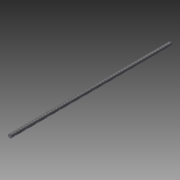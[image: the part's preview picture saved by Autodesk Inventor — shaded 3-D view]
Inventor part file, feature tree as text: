
AUTODESK INVENTOR PART (.ipt)
format: ipt  version: 2014 SP1 (Build 180222100, 222)  size: 68,096 bytes
history: native  units: mm
features: extrude x1, thread x1, sketch x1
ambient origin geometry x8: Origin, YZ Plane, XZ Plane, XY Plane, X Axis, Y Axis, Z Axis, Center Point
bodies: Solid1 (feature_tree)
feature tree (3):
  extrude  "Extrusion1"  Depth=350.0mm TaperAngle=0.0deg
  thread  "Thread1"  [1 undecoded]
  sketch  "Sketch1"  dims[d0=8.0mm d1=350.0mm d2=0.0mm d3=10.0mm d4=0.0mm]
note: 1 required parameter value undecoded (feature->parameter linkage not recoverable at this tier; creation-order binding heuristic only, values carry confidence <= 0.55)
